# Revit family: RN 80041 Optipress-Aquaplus-Vis de rappel
name_source: partatom
category: Rohrformteile
units: mm (PartAtom-declared; Revit-internal decimal feet)

## family parameters
Arbeitsebenenbasiert = Nein
Beim Laden mit Abzugskörper schneiden = Nein
Bemaßung runder Anschluss = Durchmesser verwenden
Gemeinsam genutzt = Nein
Immer vertikal = Ja
Teiletyp = Verbindung

## types (7) — shared parameters
1.010.00.2 Numéro de feuille de la directive = 29
1.010.00.3 Date de publication (mois) de la ligne directrice = 201308
1.010.00.4 Nom du Fabricant = R. Nussbaum AG
1.010.00.5 Date de révision du fichier = 20190521
1.010.00.6 Adresse Web du fabricant = http://www.nussbaum.ch
1.100.00.4 Désignation du produit = Alimentation
1.110.00.2 Indice = 4
1.110.00.4 Désignation du produit = Optipress
1.960/3L.00.8 Lien (URL) = https://www.nussbaum.ch
29.700.00.4 Nom du produit = Optipress-Aquaplus-Vis de rappel
29.700.00.5 Identification du produit = 2
29.700.00.6 Forme transversale = 1
29.700.00.7 Système de taille nominale = DN
29.700.00.8 Système de pression nominale = PN
29.710.02.4 Pression nominale = 16
29.710.02.5 Max. [hPa] = 1600
29.710.02.7 Max. [hPa] = 1600
29.710.02.9 Max. [°C] = 95
Connector Visibility = Nein
EnclosingSpace Visibility = Nein

## per-type parameters (varying)
| type | 1.800.00.3 Numéro BS | 1.810.00.3 Numéro de commande fabricant | 1.810.00.4 Numéro DATANORM | 1.810.00.5 Numéro StLB | 1.810.00.6 Numéro GTIN | 29.710.02.10 Poids d'ajustement [kg] | 29.710.02.3 La désignation | CONNECTOR0_DIAMETER_dX_0r | CONNECTOR0_dX_01 | CONNECTOR0_ref_dX | CONNECTOR1_DIAMETER_dX_0r | CONNECTOR1_dX_00 | CONNECTOR1_dX_01 | CONNECTOR1_ref_dX | R. Nussbaum AG 80041.22 fr Visibility | R. Nussbaum AG 80041.23 fr Visibility | R. Nussbaum AG 80041.24 fr Visibility | R. Nussbaum AG 80041.25 fr Visibility | R. Nussbaum AG 80041.26 fr Visibility | R. Nussbaum AG 80041.27 fr Visibility | R. Nussbaum AG 80041.28 fr Visibility |
| 80041.22, Optipress-Aquaplus-Vis de rappel, DN=12, L=86 | 01900400000000000000000000000000000000000000000026000000000000000001 | 80041.22 | 80041.22 | 266.312 | 7612945602404 | 0.15 | Optipress-Aquaplus-Vis de rappel, DN=12, L=86 | 12 mm  [stored 0.0393701 ft] | 22 mm | 22 mm | 12 mm  [stored 0.0393701 ft] | 64 mm | 86 mm | 64 mm | Ja | Nein | Nein | Nein | Nein | Nein | Nein |
| 80041.23, Optipress-Aquaplus-Vis de rappel, DN=15, L=85 | 01900400000000000000000000000000000000000000000026000000000000000002 | 80041.23 | 80041.23 | 266.313 | 7612945602411 | 0.139 | Optipress-Aquaplus-Vis de rappel, DN=15, L=85 | 15 mm  [stored 0.0492126 ft] | 22 mm | 22 mm | 15 mm  [stored 0.0492126 ft] | 63 mm | 85 mm | 63 mm | Nein | Ja | Nein | Nein | Nein | Nein | Nein |
| 80041.24, Optipress-Aquaplus-Vis de rappel, DN=20, L=94 | 01900400000000000000000000000000000000000000000026000000000000000003 | 80041.24 | 80041.24 | 266.314 | 7612945602428 | 0.21 | Optipress-Aquaplus-Vis de rappel, DN=20, L=94 | 20 mm | 24 mm | 24 mm | 20 mm | 70 mm | 94 mm | 70 mm | Nein | Nein | Ja | Nein | Nein | Nein | Nein |
| 80041.25, Optipress-Aquaplus-Vis de rappel, DN=25, L=100 | 01900400000000000000000000000000000000000000000026000000000000000004 | 80041.25 | 80041.25 | 266.315 | 7612945602435 | 0.393 | Optipress-Aquaplus-Vis de rappel, DN=25, L=100 | 25 mm  [stored 0.082021 ft] | 24 mm | 24 mm | 25 mm  [stored 0.082021 ft] | 77 mm | 101 mm | 77 mm | Nein | Nein | Nein | Ja | Nein | Nein | Nein |
| 80041.26, Optipress-Aquaplus-Vis de rappel, DN=32, L=110 | 01900400000000000000000000000000000000000000000026000000000000000005 | 80041.26 | 80041.26 | 266.316 | 7612945602442 | 0.468 | Optipress-Aquaplus-Vis de rappel, DN=32, L=110 | 32 mm | 26 mm | 26 mm | 32 mm | 85 mm | 111 mm | 85 mm | Nein | Nein | Nein | Nein | Ja | Nein | Nein |
| 80041.27, Optipress-Aquaplus-Vis de rappel, DN=40, L=139 | 01900400000000000000000000000000000000000000000026000000000000000006 | 80041.27 | 80041.27 | 266.317 | 7612945602459 | 0.678 | Optipress-Aquaplus-Vis de rappel, DN=40, L=139 | 40 mm | 36 mm | 36 mm | 40 mm | 103 mm | 139 mm | 103 mm | Nein | Nein | Nein | Nein | Nein | Ja | Nein |
| 80041.28, Optipress-Aquaplus-Vis de rappel, DN=50, L=152 | 01900400000000000000000000000000000000000000000026000000000000000007 | 80041.28 | 80041.28 | 266.318 | 7612945602466 | 1.141 | Optipress-Aquaplus-Vis de rappel, DN=50, L=152 | 50 mm | 40 mm | 40 mm | 50 mm | 112 mm | 152 mm | 112 mm | Nein | Nein | Nein | Nein | Nein | Nein | Ja |

note: column(s) folded — value = type name in every type: 1.800.00.4 Champ de commentaires

note: [stored X ft] marks values corroborated as IEEE doubles in the binary element streams (Revit-internal decimal feet)

## geometry (parser evidence)
native form markers: Sweep x2
no freeform markers — native parametric forms only
